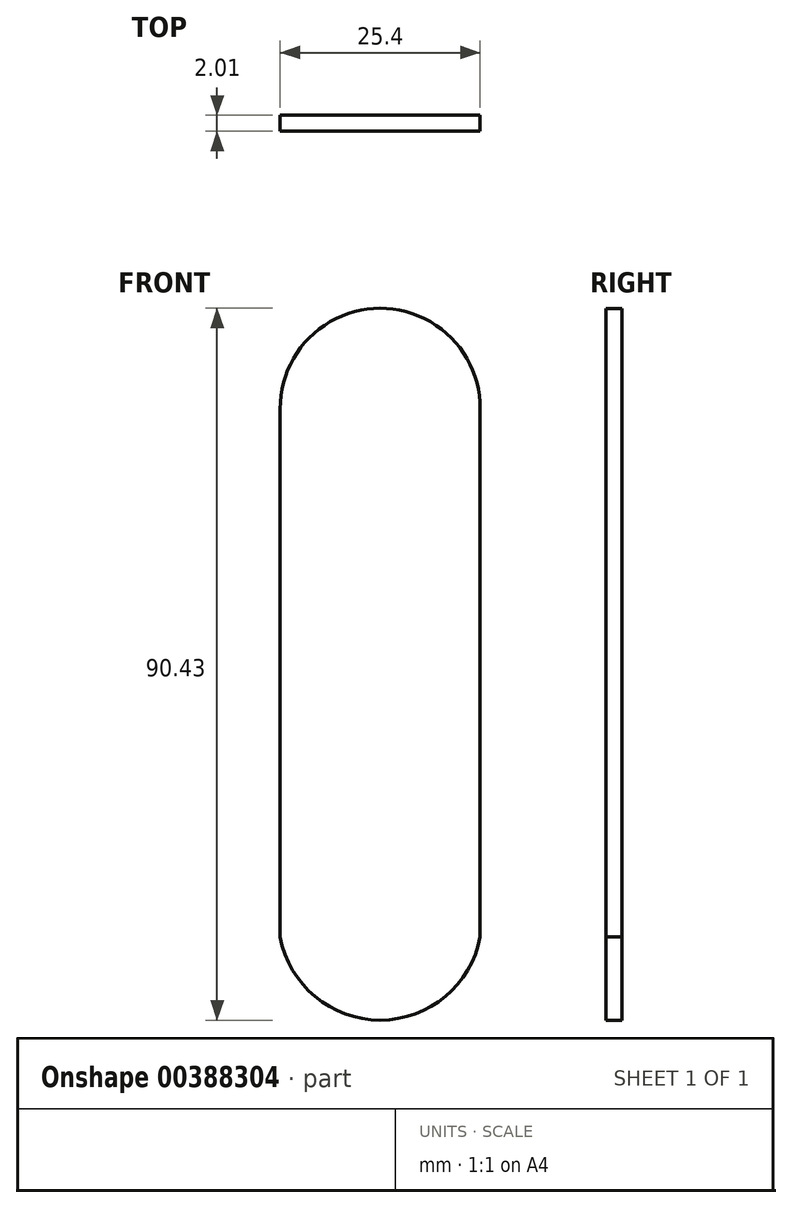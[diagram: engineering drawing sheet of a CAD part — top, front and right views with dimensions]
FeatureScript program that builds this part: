
annotation { "Feature Type Name" : "Feature", "Feature Type Description" : "" }
export const myFeature = defineFeature(function(context is Context, id is Id, definition is map)
    precondition{}
    {
        {
            var Q0;
            Q0=qCreatedBy(makeId("Front.planeOp"),FACE);
            var sketch = newSketch(context, id + "F0", { "sketchPlane" : qUnion([Q0])});
            skLineSegment(sketch, "E0", {"start": v(0, 46.3) * mm, "end": v(0, -44.13) * mm, "construction": true});
            skLineSegment(sketch, "E1", {"start": v(-12.7, 0) * mm, "end": v(0, 0) * mm, "construction": true});
            skLineSegment(sketch, "E2", {"start": v(0, 0) * mm, "end": v(12.7, 0) * mm, "construction": true});
            skLineSegment(sketch, "E3", {"start": v(-12.7, 0) * mm, "end": v(-12.7, -33.54) * mm});
            skLineSegment(sketch, "E4", {"start": v(12.7, 0) * mm, "end": v(12.7, -33.54) * mm});
            skArc(sketch, "E5", {"start": v(-12.7, -33.54) * mm, "mid": v(0, -44.13) * mm, "end": v(12.7, -33.54) * mm});
            skLineSegment(sketch, "E6", {"start": v(-12.7, 0) * mm, "end": v(-12.7, 33.53) * mm});
            skLineSegment(sketch, "E7", {"start": v(12.7, 0) * mm, "end": v(12.7, 33.53) * mm});
            skArc(sketch, "E8", {"start": v(12.7, 33.53) * mm, "mid": v(0, 46.3) * mm, "end": v(-12.7, 33.53) * mm});
            skSolve(sketch);
        }
        {
            var Q0;
            Q0=qSketchRegion(id+"F0",true);
            extrude(context, id + "F1", {"entities" : qUnion([Q0]), "depth" : 2 * mm});
        }
    });
